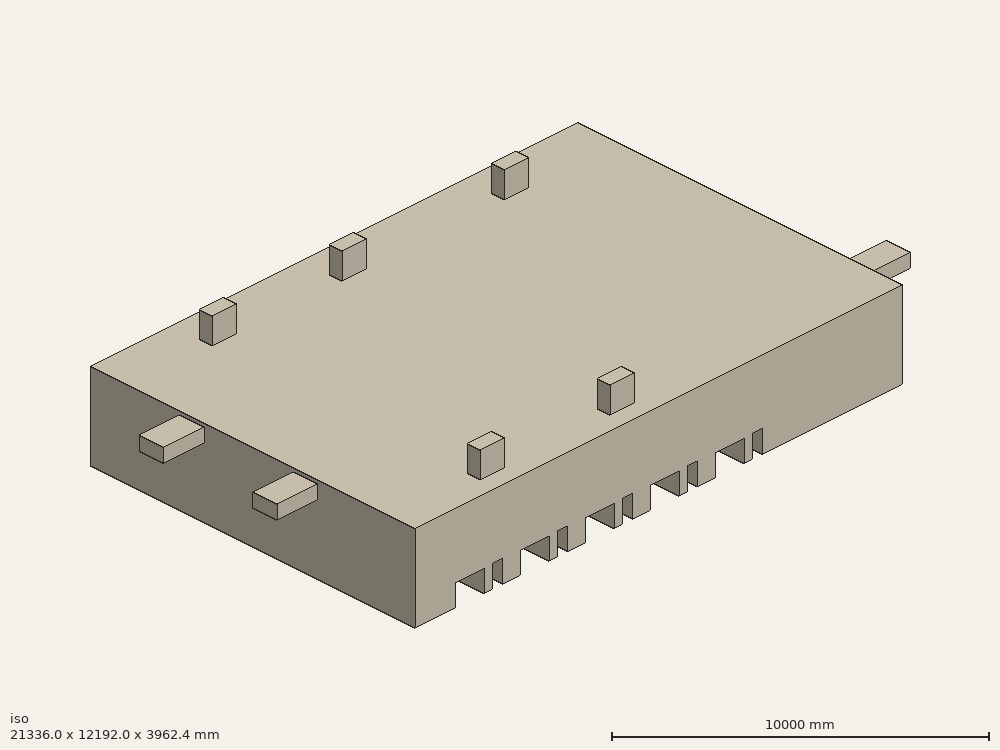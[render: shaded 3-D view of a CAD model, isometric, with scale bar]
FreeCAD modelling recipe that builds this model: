
FCSTD DOCUMENT  (FreeCAD 0.18R14555 (Git shallow))
Label: flow_domain
License: All rights reserved
LicenseURL: http://en.wikipedia.org/wiki/All_rights_reserved
objects: Part::Box×20, Part::MultiFuse×12, Part::Mirroring×1, Part::Cut×1
note: 34 computed .brp shape members not serialized (recipe doc carries the construction recipe); baked Part::Feature solids carry a one-line shape summary decoded from their .brp

FEATURE [Part::Box] Box001  label="Bed 1"
  AttacherType = Attacher::AttachEngine3D
  Height = 762
  Length = 1066.8
  Width = 1981.2
FEATURE [Part::Box] Box002  label="Table 1"
  AttacherType = Attacher::AttachEngine3D
  Height = 798.576
  Length = 396.24
  Placement = pos=(1371.6,0,0) rot=(0,0,1;0rad)
  Width = 396.24
FEATURE [Part::MultiFuse] Fusion  label="Set 1"
  Shapes = -> [Box002,Box001]
FEATURE [Part::Box] Box003  label="Bed 002"
  AttacherType = Attacher::AttachEngine3D
  Height = 762
  Length = 1066.8
  Width = 1981.2
FEATURE [Part::Box] Box004  label="Table 002"
  AttacherType = Attacher::AttachEngine3D
  Height = 798.576
  Length = 396.24
  Placement = pos=(1371.6,0,0) rot=(0,0,1;0rad)
  Width = 396.24
FEATURE [Part::MultiFuse] Fusion001  label="Set 2"
  Placement = pos=(2438.4,0,0) rot=(0,0,1;0rad)
  Shapes = -> [Box004,Box003]
FEATURE [Part::Box] Box005  label="Table 003"
  AttacherType = Attacher::AttachEngine3D
  Height = 798.576
  Length = 396.24
  Placement = pos=(1371.6,0,0) rot=(0,0,1;0rad)
  Width = 396.24
FEATURE [Part::Box] Box006  label="Bed 003"
  AttacherType = Attacher::AttachEngine3D
  Height = 762
  Length = 1066.8
  Width = 1981.2
FEATURE [Part::MultiFuse] Fusion002  label="Set 3"
  Placement = pos=(4876.8,0,0) rot=(0,0,1;0rad)
  Shapes = -> [Box005,Box006]
FEATURE [Part::Box] Box007  label="Bed 004"
  AttacherType = Attacher::AttachEngine3D
  Height = 762
  Length = 1066.8
  Width = 1981.2
FEATURE [Part::Box] Box008  label="Table 004"
  AttacherType = Attacher::AttachEngine3D
  Height = 798.576
  Length = 396.24
  Placement = pos=(1371.6,0,0) rot=(0,0,1;0rad)
  Width = 396.24
FEATURE [Part::MultiFuse] Fusion003  label="Set 4"
  Placement = pos=(7315.2,0,0) rot=(0,0,1;0rad)
  Shapes = -> [Box008,Box007]
FEATURE [Part::Box] Box009  label="Table 005"
  AttacherType = Attacher::AttachEngine3D
  Height = 798.576
  Length = 396.24
  Placement = pos=(1371.6,0,0) rot=(0,0,1;0rad)
  Width = 396.24
FEATURE [Part::Box] Box010  label="Bed 005"
  AttacherType = Attacher::AttachEngine3D
  Height = 762
  Length = 1066.8
  Width = 1981.2
FEATURE [Part::MultiFuse] Fusion004  label="Set 5"
  Placement = pos=(9753.6,0,0) rot=(0,0,1;0rad)
  Shapes = -> [Box009,Box010]
FEATURE [Part::MultiFuse] Fusion005  label="right beds"
  Shapes = -> [Fusion001,Fusion002,Fusion003,Fusion004,Fusion]
FEATURE [Part::Mirroring] Part__Mirroring  label="left beds"
  Base = (0,6096,0)
  Normal = (0,1,0)
  Source = -> Fusion005
FEATURE [Part::Box] Box011  label="Nurse Station"
  AttacherType = Attacher::AttachEngine3D
  Height = 1219.2
  Length = 3048
  Placement = pos=(15240,7620,0) rot=(0,0,1;0rad)
  Width = 4572
FEATURE [Part::Box] Box012  label="main inlet"
  AttacherType = Attacher::AttachEngine3D
  Height = 487.68
  Length = 2438.4
  Placement = pos=(17373.6,1219.2,2438.4) rot=(0,0,1;0rad)
  Width = 914.4
FEATURE [Part::Box] Box013  label="main outlet"
  AttacherType = Attacher::AttachEngine3D
  Height = 487.68
  Length = 2438.4
  Placement = pos=(-1524,3657.6,2438.4) rot=(0,0,1;0rad)
  Width = 914.4
FEATURE [Part::Box] Box014  label="branch"
  AttacherType = Attacher::AttachEngine3D
  Height = 1219.2
  Length = 914.4
  Placement = pos=(14020.8,10668,2743.2) rot=(0,0,1;0rad)
  Width = 487.68
FEATURE [Part::Box] Box016  label="branch002"
  AttacherType = Attacher::AttachEngine3D
  Height = 1219.2
  Length = 914.4
  Placement = pos=(7924.8,609.6,2743.2) rot=(0,0,1;0rad)
  Width = 487.68
FEATURE [Part::Box] Box017  label="branch003"
  AttacherType = Attacher::AttachEngine3D
  Height = 1219.2
  Length = 914.4
  Placement = pos=(7924.8,10668,2743.2) rot=(0,0,1;0rad)
  Width = 487.68
FEATURE [Part::Box] Box018  label="branch004"
  AttacherType = Attacher::AttachEngine3D
  Height = 1219.2
  Length = 914.4
  Placement = pos=(3048,609.6,2743.2) rot=(0,0,1;0rad)
  Width = 487.68
FEATURE [Part::Box] Box019  label="branch005"
  AttacherType = Attacher::AttachEngine3D
  Height = 1219.2
  Length = 914.4
  Placement = pos=(3048,10668,2743.2) rot=(0,0,1;0rad)
  Width = 487.68
FEATURE [Part::MultiFuse] Fusion006  label="all beds"
  Placement = pos=(1524,0,0) rot=(0,0,1;0rad)
  Shapes = -> [Part__Mirroring,Fusion005]
FEATURE [Part::Box] Box  label="Room"
  AttacherType = Attacher::AttachEngine3D
  Height = 3048
  Length = 18288
  Width = 12192
FEATURE [Part::Box] Box020  label="main outlet001"
  AttacherType = Attacher::AttachEngine3D
  Height = 487.68
  Length = 2438.4
  Placement = pos=(-1524,7924.8,2438.4) rot=(0,0,1;0rad)
  Width = 914.4
FEATURE [Part::MultiFuse] Fusion007  label="main_ducts"
  Shapes = -> [Box020,Box013,Box012]
FEATURE [Part::MultiFuse] Fusion008  label="branch_ducts"
  Shapes = -> [Box014,Box016,Box017,Box018,Box019]
FEATURE [Part::MultiFuse] Fusion009  label="vents"
  Shapes = -> [Fusion008,Fusion007]
FEATURE [Part::MultiFuse] Fusion010  label="surfaces"
  Shapes = -> [Fusion006,Box011]
FEATURE [Part::MultiFuse] Fusion011
  Shapes = -> [Box,Fusion009]
FEATURE [Part::Cut] Cut
  Base = -> Fusion011
  Tool = -> Fusion010
